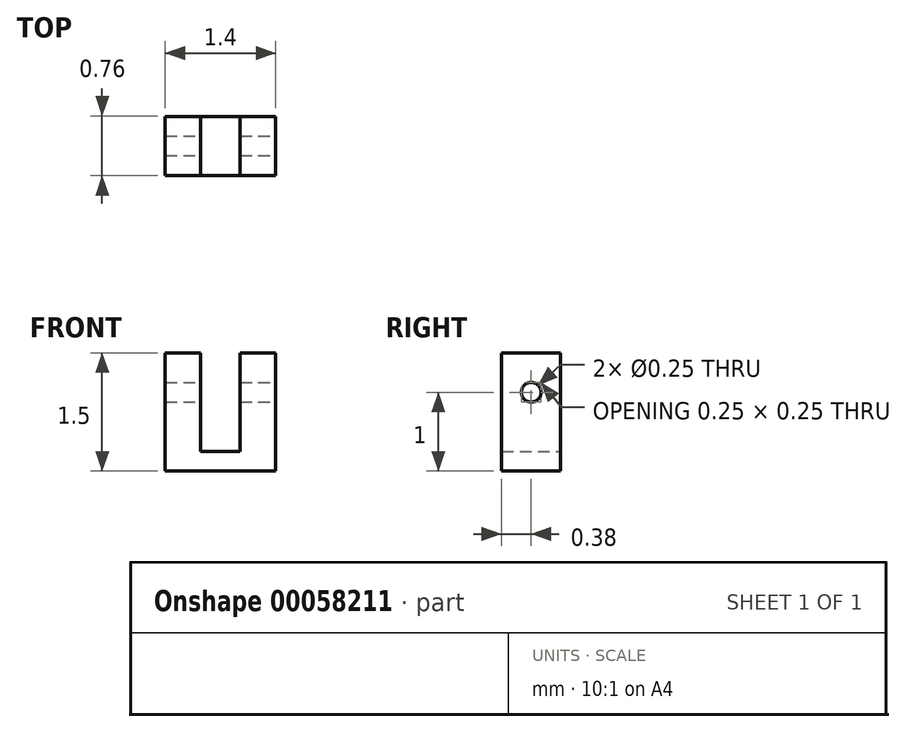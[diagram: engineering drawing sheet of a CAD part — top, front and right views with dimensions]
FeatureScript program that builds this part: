
annotation { "Feature Type Name" : "Feature", "Feature Type Description" : "" }
export const myFeature = defineFeature(function(context is Context, id is Id, definition is map)
    precondition{}
    {
        {
            var Q0;
            Q0=qCreatedBy(makeId("Front.planeOp"),FACE);
            var sketch = newSketch(context, id + "F0", { "sketchPlane" : qUnion([Q0])});
            skLineSegment(sketch, "E0", {"start": v(0, 0) * mm, "end": v(0.7, 0) * mm});
            skLineSegment(sketch, "E1", {"start": v(0.7, 0) * mm, "end": v(0.7, 1.5) * mm});
            skLineSegment(sketch, "E2", {"start": v(0.7, 1.5) * mm, "end": v(0.25, 1.5) * mm});
            skLineSegment(sketch, "E3", {"start": v(0.25, 1.5) * mm, "end": v(0.25, 0.25) * mm});
            skLineSegment(sketch, "E4", {"start": v(0.25, 0.25) * mm, "end": v(-0.25, 0.25) * mm});
            skLineSegment(sketch, "E5", {"start": v(-0.25, 0.25) * mm, "end": v(-0.25, 1.5) * mm});
            skLineSegment(sketch, "E6", {"start": v(-0.25, 1.5) * mm, "end": v(-0.7, 1.5) * mm});
            skLineSegment(sketch, "E7", {"start": v(-0.7, 1.5) * mm, "end": v(-0.7, 0) * mm});
            skLineSegment(sketch, "E8", {"start": v(-0.7, 0) * mm, "end": v(0, 0) * mm});
            skSolve(sketch);
        }
        {
            var Q0;
            Q0 = qSketchRegion(id + "F0", true);
            extrude(context, id + "F1", {"entities" : qUnion([Q0]), "depth" : (0.75 / 2) * mm, "hasSecondDirection" : true, "secondDirectionOppositeDirection" : true, "secondDirectionDepth" : (0.75 / 2) * mm});
        }
        {
            var Q0;
            Q0=qCreatedBy(makeId("Right.planeOp"),FACE);
            var sketch = newSketch(context, id + "F2", { "sketchPlane" : qUnion([Q0])});
            skCircle(sketch, "E9", {"center": v(0, 1) * mm, "radius": 0.13 * mm});
            skSolve(sketch);
        }
        {
            var Q0;
            Q0 = qSketchRegion(id + "F2", true);
            extrude(context, id + "F3", {"entities" : qUnion([Q0]), "operationType" : NewBodyOperationType.REMOVE, "oppositeDirection" : true, "depth" : 25 * mm, "hasSecondDirection" : true, "secondDirectionOppositeDirection" : false, "secondDirectionDepth" : 25 * mm});
        }
    });
